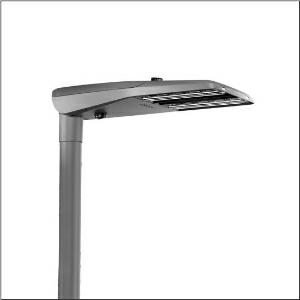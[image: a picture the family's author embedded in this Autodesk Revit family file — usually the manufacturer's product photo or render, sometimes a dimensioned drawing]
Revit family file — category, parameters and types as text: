
# Revit family: streetlight_sl_11_iq_midi___st1_0a_5xc3m51y08le_e71b
name_source: partatom
category: Lighting Fixtures
units: mm (PartAtom-declared; Revit-internal decimal feet)

## family parameters
Cut with Voids When Loaded = No
Host = Face
Light Source = No
Part Type = Normal
Room Calculation Point = No
Round Connector Dimension = Use Diameter
Shared = No

## types (1)
- --- (1 x LED, 8920 lm, 59.4 W, 3000K)
    Apparent Load = 59 VA
    CIE Flux Codes = 33 66 96 100 100
    Color Rendering = 70
    Color Temperature = 3000K
    Default Elevation = 1800 mm
    Description = Streetlight SL 11 iQ midi, mast luminaire, primary light control with 3 zone facetted reflector, of plastic, silver coated, highly specular, primary optical cover: cover, of PMMA, transparent, light distribution: ST1.0a, light emission: direct distribution, primary light characteristic: asymmetric, installation type: post-top, side-entry, lamps: LED, High Power LED, rated values: 8.920lm | 59,4W | 150,2lm/W (begin service life); end service life: 8.920lm | 61,6W; at 50% lumin. flux: 4.460lm | 28,5W | 156,5lm/W, colour temperature: 3000K, colour rendering: CRI > 70, light colour: 730, light setting 1 begin service life: 100% | 8.920lm | 59,4W | 150,2lm/W | 3.000K, light setting 1 end service life: 61,6W, further light settings possible, control: pre-setting: logarithmic dimming characteristic, Street-Remote, Auto-Match, Temp-Guard, Lumen-Switch, Night-Set, Smart-Wire, Light-Fading, Desk-Remote (wireless, voltage-free reading and setting of iQ features in the workshop via application-optimized NFC function/RFID function), optimised constant luminous flux control (CLO 2.0), with cable H07RN-F 3x 1.5mm², mains connection: 230..240V, AC, 50/60Hz, connection cable pre-assembled, cable length: 8,5m, luminaire housing, of diecast aluminium, powder-coated, SITECO metallic grey (DB 702S), please order mast flange separately, inclination adjustable without tools: 0°, 5°, 10°, 15° (post-top) | 0°, -5°, -10°, -15° (side-entry), sealing non-destructively replaceable, multi-level sealing system, length: 780mm, width: 376mm, height: 118mm, mast flange for spigot size: 42mm (side-entry): 5XC10008XM4, 60/48mm (side-entry/post-top): 5XC10108XM2, 76/60mm (side-entry/post-top): 5XC10108XM1, equipment: standard, Smart Interface below and above, protection rating (complete): IP66, insulation class (complete): insulation class II (safety insulation), certification: CE, ENEC, ENEC+, VDE, UKCA, impact resistance: IK10, permissible operating ambient temperature for outdoor applications: -25..+50°C, standard-compliant lighting for roads and squares, Environmental Product Declaration (EPD) tested and certified by an independent institute, packaging unit: 1 piece

Light Distribution: ST1.0a
    Height = 118 mm
    Lamp = 1 x LED
    Lamp Light Flux = 8920 lm
    Lamp Power = 59.4 W
    Lamp count = 1
    Length = 780 mm
    Luminous efficacy = 150 lm/W
    Manufacturer = Siteco
    ModVariant = No
    Model = 5XC3M51Y08LE
    Number of Poles = 1
    OnlyDefault = Yes
    Power Factor = 1
    Product Name = Streetlight SL 11 iQ midi | ST1.0a
    Product group = mast luminaire | pylon top
    ProductGroupID = 6100
    Protection Class = Protection class II
    Protection Degree = IP 66
    RLX_Detail_Level = 1
    RLX_Emergency_Light_Flux = 0 lm
    RLX_Emergency_Type = 0
    RLX_Emergency_Type_DB = No
    RlxData = <blob elided: 69161 chars, md5=4f8f416f>
    Socket = socket
    Standby Power = 0 W
    System Light Flux = 8920 lm
    System Power = 59 W
    Type Comments = factory setting: luminous flux: 100 % | dim-lin: 254 | 521 mA
    Type Image = l_1004429.jpg
    URL = http://relux.com
    VarID = @adj_092303
    Voltage = 0 V
    Weight = 0.00 kg
    Width = 376 mm

## geometry (parser evidence)
native form markers: Blend x4, Sweep x11
no freeform markers — native parametric forms only
